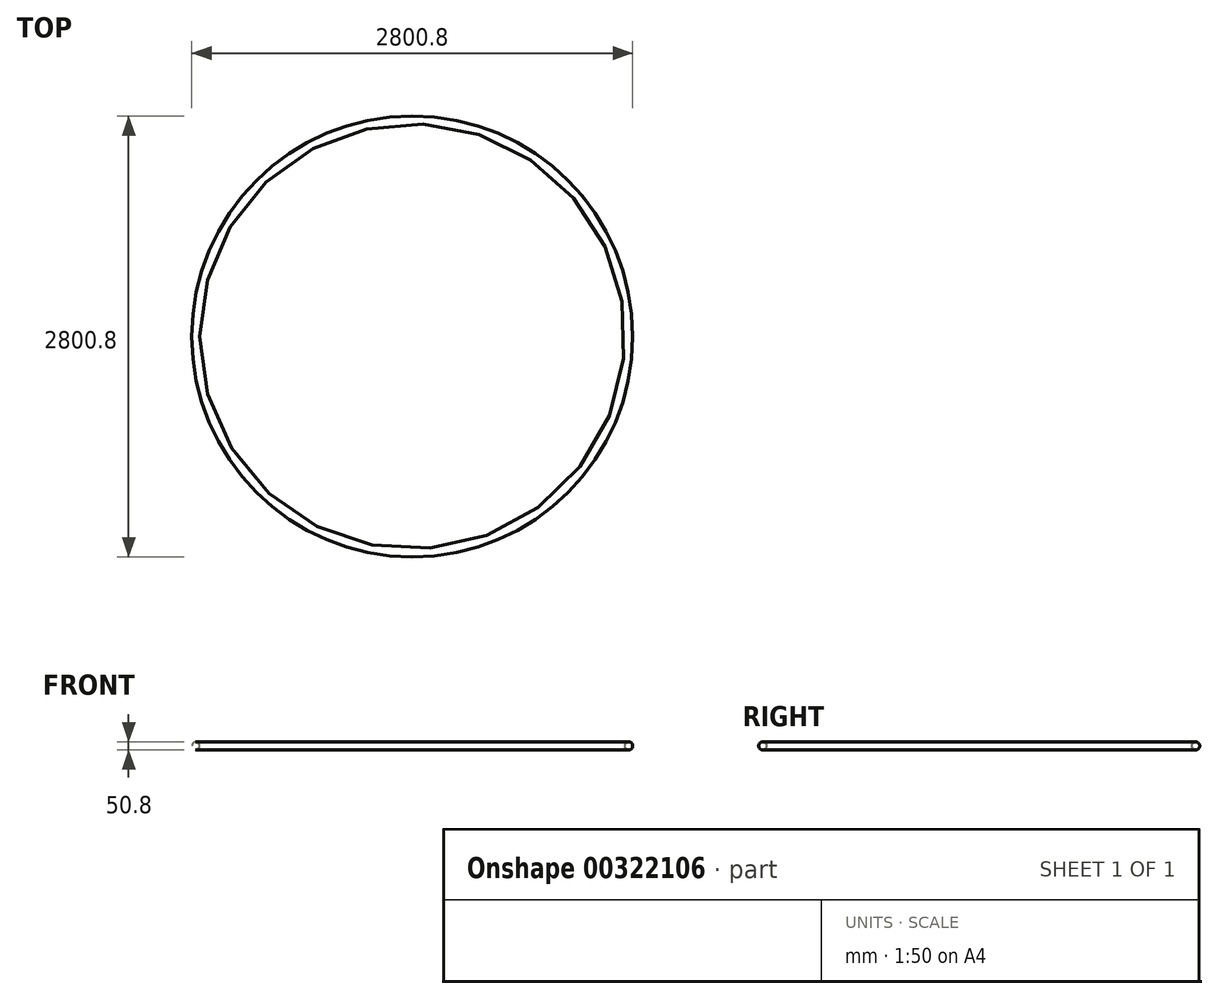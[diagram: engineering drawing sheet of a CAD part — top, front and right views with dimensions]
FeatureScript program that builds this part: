
annotation { "Feature Type Name" : "Feature", "Feature Type Description" : "" }
export const myFeature = defineFeature(function(context is Context, id is Id, definition is map)
    precondition{}
    {
        {
            var Q0;
            Q0=qCreatedBy(makeId("Front.planeOp"),FACE);
            var sketch = newSketch(context, id + "F0", { "sketchPlane" : qUnion([Q0])});
            skLineSegment(sketch, "E0", {"start": v(0, 0) * mm, "end": v(0, 82.52) * mm, "construction": true});
            skCircle(sketch, "E1", {"center": v(-1375, 0) * mm, "radius": 25.4 * mm});
            skCircle(sketch, "E2.0", {"center": v(-1375, 0) * mm, "radius": 23.4 * mm});
            skSolve(sketch);
        }
        {
            var Q0;
            Q0 = qSketchRegion(id + "F0", true);
            var Q1;
            Q1=sQuery(id+"F0.wireOp",EDGE,"E0");
            revolve(context, id + "F1", {"entities" : qUnion([Q0]), "axis" : qUnion([Q1]), "revolveType" : RevolveType.FULL});
        }
    });
